# Revit family: DS2P
name_source: partatom
category: Air Terminals
revit_build: Autodesk Revit MEP 2012 (Build: 20110309_2315(x64)
units: mm (PartAtom-declared; Revit-internal decimal feet)

## types (6) — shared parameters
Manufacturer = INNES
Máxima presión total = 0.00 in-wg
Máxima velocidad de cuello = 0 FPM
Mínima presión total = 0.00 in-wg
Mínima velocidad de cuello = 0 FPM
URL = http://www.innes.com.mx

## per-type parameters (varying)
| type | B2 | C int 2 | C2 | D | D2 | E | E2 | Eje ventilas | G2 | Height | RA | Width | a2 | b2 | c2 | g2 |
| DS2P-06 | 7 19/32" | 2 15/16" | 6" | 21 3/16" | 1 1/2" | 11 3/16" | 3 11/16" | 9 19/32" | 2 15/16" | 12 5/8" | 3 1/8" | 22 5/8" | 3 1/8" | 3 51/64" | 3" | 1 15/32" |
| DS2P-08 | 9 13/16" | 3 59/64" | 7 31/32" | 25 3/16" | 1 3/4" | 13 3/16" | 4 11/16" | 11 19/32" | 3 15/16" | 14 5/8" | 4 7/64" | 26 5/8" | 4 7/64" | 4 29/32" | 3 63/64" | 1 31/32" |
| DS2P-10 | 12 23/32" | 5 15/64" | 10 19/32" | 31 3/16" | 2 1/16" | 17 3/16" | 6 23/32" | 14 19/32" | 5 1/2" | 18 5/8" | 5 27/64" | 32 5/8" | 5 27/64" | 6 23/64" | 5 19/64" | 2 3/4" |
| DS2P-12 | 14 3/16" | 5 31/32" | 12 1/16" | 35 3/16" | 2 7/16" | 19 3/16" | 7 7/8" | 16 19/32" | 6 1/2" | 20 5/8" | 6 5/32" | 36 5/8" | 6 5/32" | 7 3/32" | 6 1/32" | 3 1/4" |
| DS2P-16 | 18 3/4" | 8 1/16" | 16 1/4" | 43 3/16" | 4 11/32" | 23 3/16" | 9 17/32" | 20 19/32" | 9 1/32" | 24 5/8" | 8 1/4" | 44 5/8" | 8 1/4" | 9 3/8" | 8 1/8" | 4 33/64" |
| DS2P-20 | 21 1/16" | 9 15/64" | 18 19/32" | 49 3/16" | 3 25/32" | 25 3/16" | 11 17/32" | 23 19/32" | 12 7/32" | 26 5/8" | 9 27/64" | 50 5/8" | 9 27/64" | 10 17/32" | 9 19/64" | 6 7/64" |

## geometry (parser evidence)
native form markers: Sweep x5
no freeform markers — native parametric forms only
